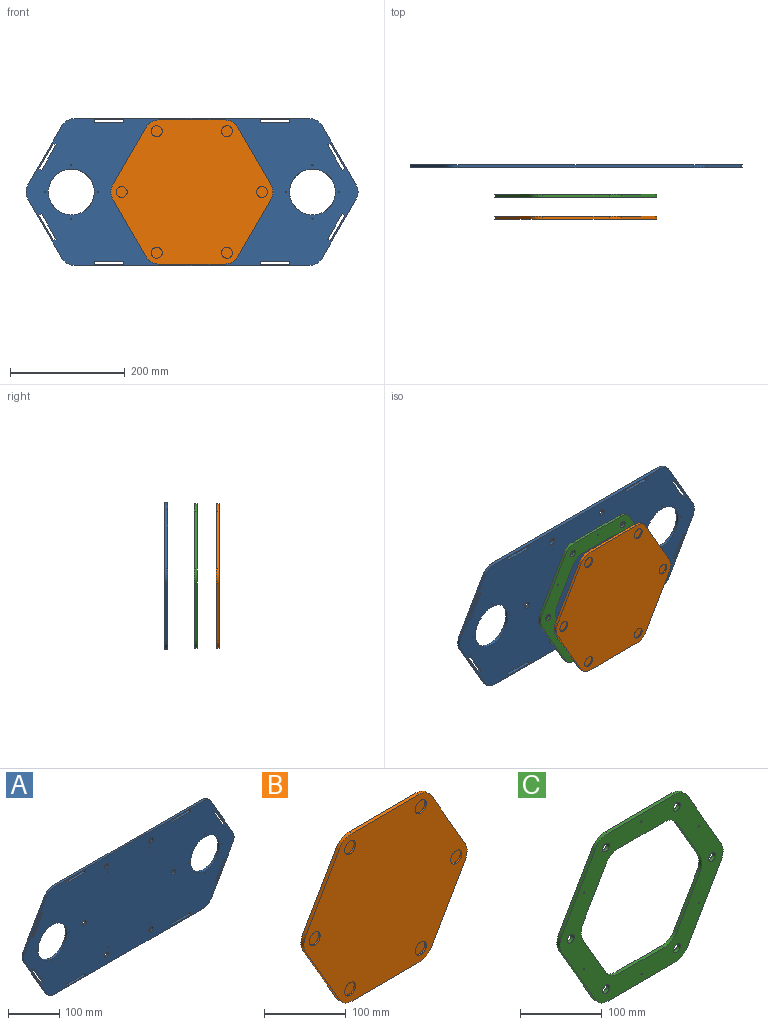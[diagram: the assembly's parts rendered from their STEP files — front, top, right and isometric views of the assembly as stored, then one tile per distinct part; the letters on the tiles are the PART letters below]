
ASSEMBLY  parts=3 mates=3
PART A: 66 faces, bbox 579.1x5.1x256.5 mm
  f0: plane 579.12x256.54mm, normal (0,-1,0), area 118440.4mm2, adj f2,f3,f4,f5,f6,f7,f8,f9
  f1: plane 579.12x256.54mm, normal (0,1,0), area 118440.4mm2, adj f2,f3,f4,f5,f6,f7,f8,f9
  f2: cylinder r=1.02mm len=5.08mm, axis (0,-1,0), area 32.4mm2, adj f0,f1
  f3: cylinder r=1.02mm len=5.08mm, axis (0,-1,0), area 32.4mm2, adj f0,f1
  f4: cylinder r=1.02mm len=5.08mm, axis (0,-1,0), area 32.4mm2, adj f0,f1
  f5: cylinder r=1.02mm len=5.08mm, axis (0,-1,0), area 32.4mm2, adj f0,f1
  f6: cylinder r=5.99mm len=11.99mm, axis (0,-1,0), area 191.3mm2, adj f0,f1
  f7: cylinder r=5.99mm len=11.99mm, axis (0,-1,0), area 191.3mm2, adj f0,f1
  f8: cylinder r=5.99mm len=11.99mm, axis (0,-1,0), area 191.3mm2, adj f0,f1
  f9: cylinder r=5.99mm len=11.99mm, axis (0,-1,0), area 191.3mm2, adj f0,f1
  f10: cylinder r=5.99mm len=11.99mm, axis (0,-1,0), area 191.3mm2, adj f0,f1
  f11: cylinder r=5.99mm len=11.99mm, axis (0,-1,0), area 191.3mm2, adj f0,f1
  f12: cylinder r=40mm len=80mm, axis (0,-1,0), area 1276.7mm2, adj f0,f1
  f13: cylinder r=1.02mm len=5.08mm, axis (0,-1,0), area 32.4mm2, adj f0,f1
  f14: cylinder r=1.02mm len=5.08mm, axis (0,-1,0), area 32.4mm2, adj f0,f1
  f15: cylinder r=1.02mm len=5.08mm, axis (0,-1,0), area 32.4mm2, adj f0,f1
  f16: cylinder r=1.02mm len=5.08mm, axis (0,-1,0), area 32.4mm2, adj f0,f1
  f17: cylinder r=40mm len=80mm, axis (0,-1,0), area 1276.7mm2, adj f0,f1
  f18: cylinder r=1.02mm len=5.08mm, axis (0,-1,0), area 32.4mm2, adj f0,f1
  f19: cylinder r=1.02mm len=5.08mm, axis (0,-1,0), area 32.4mm2, adj f0,f1
  f20: cylinder r=1.02mm len=5.08mm, axis (0,-1,0), area 32.4mm2, adj f0,f1
  f21: cylinder r=1.02mm len=5.08mm, axis (0,-1,0), area 32.4mm2, adj f0,f1
  f22: plane 5.33x5.08mm, normal (-1,0,0), area 27.1mm2, adj f0,f1,f24,f47
  f23: plane 5.33x5.08mm, normal (1,0,0), area 27.1mm2, adj f0,f1,f24,f47
  f24: plane 50.8x5.08mm, normal (0,0,1), area 258.1mm2, adj f0,f1,f22,f23
  f25: plane 5.08x4.62mm, normal (-0.5,0,-0.87), area 27.1mm2, adj f0,f1,f27,f53
  f26: plane 5.08x4.62mm, normal (0.5,0,0.87), area 27.1mm2, adj f0,f1,f27,f53
  f27: plane 43.99x25.4mm, normal (-0.87,0,0.5), area 258.1mm2, adj f0,f1,f25,f26
  f28: plane 5.08x4.62mm, normal (0.5,0,-0.87), area 27.1mm2, adj f0,f1,f30,f52
  f29: plane 5.08x4.62mm, normal (-0.5,0,0.87), area 27.1mm2, adj f0,f1,f30,f52
  f30: plane 43.99x25.4mm, normal (-0.87,0,-0.5), area 258.1mm2, adj f0,f1,f28,f29
  f31: plane 5.33x5.08mm, normal (1,0,0), area 27.1mm2, adj f0,f1,f33,f50
  f32: plane 5.33x5.08mm, normal (-1,0,0), area 27.1mm2, adj f0,f1,f33,f50
  f33: plane 50.8x5.08mm, normal (0,0,-1), area 258.1mm2, adj f0,f1,f31,f32
  f34: plane 5.33x5.08mm, normal (1,0,0), area 27.1mm2, adj f0,f1,f35,f46
  f35: plane 50.8x5.08mm, normal (0,0,1), area 258.1mm2, adj f0,f1,f34,f36
  f36: plane 5.33x5.08mm, normal (-1,0,0), area 27.1mm2, adj f0,f1,f35,f46
  f37: plane 5.08x4.62mm, normal (0.5,0,-0.87), area 27.1mm2, adj f0,f1,f38,f48
  f38: plane 43.99x25.4mm, normal (0.87,0,0.5), area 258.1mm2, adj f0,f1,f37,f39
  f39: plane 5.08x4.62mm, normal (-0.5,0,0.87), area 27.1mm2, adj f0,f1,f38,f48
  f40: plane 5.08x4.62mm, normal (-0.5,0,-0.87), area 27.1mm2, adj f0,f1,f41,f49
  f41: plane 43.99x25.4mm, normal (0.87,0,-0.5), area 258.1mm2, adj f0,f1,f40,f42
  f42: plane 5.08x4.62mm, normal (0.5,0,0.87), area 27.1mm2, adj f0,f1,f41,f49
  f43: plane 5.33x5.08mm, normal (-1,0,0), area 27.1mm2, adj f0,f1,f44,f51
  f44: plane 50.8x5.08mm, normal (0,0,-1), area 258.1mm2, adj f0,f1,f43,f45
  f45: plane 5.33x5.08mm, normal (1,0,0), area 27.1mm2, adj f0,f1,f44,f51
  f46: plane 50.8x5.08mm, normal (0,0,-1), area 258.1mm2, adj f0,f1,f34,f36
  f47: plane 50.8x5.08mm, normal (0,0,-1), area 258.1mm2, adj f0,f1,f22,f23
  f48: plane 43.99x25.4mm, normal (-0.87,0,-0.5), area 258.1mm2, adj f0,f1,f37,f39
  f49: plane 43.99x25.4mm, normal (-0.87,0,0.5), area 258.1mm2, adj f0,f1,f40,f42
  f50: plane 50.8x5.08mm, normal (0,0,1), area 258.1mm2, adj f0,f1,f31,f32
  f51: plane 50.8x5.08mm, normal (0,0,1), area 258.1mm2, adj f0,f1,f43,f45
  f52: plane 43.99x25.4mm, normal (0.87,0,0.5), area 258.1mm2, adj f0,f1,f28,f29
  f53: plane 43.99x25.4mm, normal (0.87,0,-0.5), area 258.1mm2, adj f0,f1,f25,f26
  f54: plane 409.54x5.08mm, normal (0,0,-1), area 2080.5mm2, adj f0,f1,f55,f65
  f55: cylinder r=25.4mm len=22mm, axis (0,-1,0), area 135.1mm2, adj f0,f1,f54,f56
  f56: plane 102.87x59.39mm, normal (0.87,0,-0.5), area 603.4mm2, adj f0,f1,f55,f57
  f57: cylinder r=25.4mm len=25.4mm, axis (0,-1,0), area 135.1mm2, adj f0,f1,f56,f58
  f58: plane 102.87x59.39mm, normal (0.87,0,0.5), area 603.4mm2, adj f0,f1,f57,f59
  f59: cylinder r=25.4mm len=22mm, axis (0,-1,0), area 135.1mm2, adj f0,f1,f58,f60
  f60: plane 409.54x5.08mm, normal (0,0,1), area 2080.5mm2, adj f0,f1,f59,f61
  f61: cylinder r=25.4mm len=22mm, axis (0,-1,0), area 135.1mm2, adj f0,f1,f60,f62
  f62: plane 102.87x59.39mm, normal (-0.87,0,0.5), area 603.4mm2, adj f0,f1,f61,f63
  f63: cylinder r=25.4mm len=25.4mm, axis (0,-1,0), area 135.1mm2, adj f0,f1,f62,f64
  f64: plane 102.87x59.39mm, normal (-0.87,0,-0.5), area 603.4mm2, adj f0,f1,f63,f65
  f65: cylinder r=25.4mm len=22mm, axis (0,-1,0), area 135.1mm2, adj f0,f1,f54,f64
PART B: 26 faces, bbox 282.5x5.1x251.5 mm
  f0: plane 115.85x5.08mm, normal (0,0,-1), area 588.5mm2, adj f1,f11,f12,f13
  f1: cylinder r=25.4mm len=22mm, axis (0,1,0), area 135.1mm2, adj f0,f2,f12,f13
  f2: plane 100.33x57.93mm, normal (0.87,0,-0.5), area 588.5mm2, adj f1,f3,f12,f13
  f3: cylinder r=25.4mm len=25.4mm, axis (0,1,0), area 135.1mm2, adj f2,f4,f12,f13
  f4: plane 100.33x57.93mm, normal (0.87,0,0.5), area 588.5mm2, adj f3,f5,f12,f13
  f5: cylinder r=25.4mm len=22mm, axis (0,1,0), area 135.1mm2, adj f4,f6,f12,f13
  f6: plane 115.85x5.08mm, normal (0,0,1), area 588.5mm2, adj f5,f7,f12,f13
  f7: cylinder r=25.4mm len=22mm, axis (0,1,0), area 135.1mm2, adj f6,f8,f12,f13
  f8: plane 100.33x57.93mm, normal (-0.87,0,0.5), area 588.5mm2, adj f7,f9,f12,f13
  f9: cylinder r=25.4mm len=25.4mm, axis (0,1,0), area 135.1mm2, adj f8,f10,f12,f13
  f10: plane 100.33x57.93mm, normal (-0.87,0,-0.5), area 588.5mm2, adj f9,f11,f12,f13
  f11: cylinder r=25.4mm len=22mm, axis (0,1,0), area 135.1mm2, adj f0,f10,f12,f13
  f12: plane 282.5x251.46mm, normal (0,-1,0), area 52842.4mm2, adj f0,f1,f2,f3,f4,f5,f6,f7
  f13: plane 282.5x251.46mm, normal (0,1,0), area 54552.6mm2, adj f0,f1,f2,f3,f4,f5,f6,f7
  f14: cylinder r=9.53mm len=19.05mm, axis (0,-1,0), area 152mm2, adj f12,f15
  f15: plane 19.05x19.05mm, normal (0,-1,0), area 285mm2, adj f14
  f16: cylinder r=9.53mm len=19.05mm, axis (0,-1,0), area 152mm2, adj f12,f17
  f17: plane 19.05x19.05mm, normal (0,-1,0), area 285mm2, adj f16
  f18: cylinder r=9.53mm len=19.05mm, axis (0,-1,0), area 152mm2, adj f12,f19
  f19: plane 19.05x19.05mm, normal (0,-1,0), area 285mm2, adj f18
  f20: cylinder r=9.53mm len=19.05mm, axis (0,-1,0), area 152mm2, adj f12,f21
  f21: plane 19.05x19.05mm, normal (0,-1,0), area 285mm2, adj f20
  f22: cylinder r=9.53mm len=19.05mm, axis (0,-1,0), area 152mm2, adj f12,f23
  f23: plane 19.05x19.05mm, normal (0,-1,0), area 285mm2, adj f22
  f24: cylinder r=9.53mm len=19.05mm, axis (0,-1,0), area 152mm2, adj f12,f25
  f25: plane 19.05x19.05mm, normal (0,-1,0), area 285mm2, adj f24
PART C: 38 faces, bbox 282.5x5.1x251.5 mm
  f0: cylinder r=25.4mm len=22mm, axis (0,1,0), area 135.1mm2, adj f1,f23,f24,f25
  f1: plane 68.58x39.59mm, normal (0.87,0,0.5), area 402.3mm2, adj f0,f2,f24,f25
  f2: cylinder r=25.4mm len=25.4mm, axis (0,1,0), area 135.1mm2, adj f1,f3,f24,f25
  f3: plane 68.58x39.59mm, normal (0.87,0,-0.5), area 402.3mm2, adj f2,f4,f24,f25
  f4: cylinder r=25.4mm len=22mm, axis (0,1,0), area 135.1mm2, adj f3,f5,f24,f25
  f5: plane 79.19x5.08mm, normal (0,0,-1), area 402.3mm2, adj f4,f6,f24,f25
  f6: cylinder r=25.4mm len=22mm, axis (0,1,0), area 135.1mm2, adj f5,f7,f24,f25
  f7: plane 68.58x39.59mm, normal (-0.87,0,-0.5), area 402.3mm2, adj f6,f8,f24,f25
  f8: cylinder r=25.4mm len=25.4mm, axis (0,1,0), area 135.1mm2, adj f7,f9,f24,f25
  f9: plane 68.58x39.59mm, normal (-0.87,0,0.5), area 402.3mm2, adj f8,f10,f24,f25
  f10: cylinder r=25.4mm len=22mm, axis (0,1,0), area 135.1mm2, adj f9,f23,f24,f25
  f11: plane 115.85x5.08mm, normal (0,0,-1), area 588.5mm2, adj f12,f22,f24,f25
  f12: cylinder r=25.4mm len=22mm, axis (0,1,0), area 135.1mm2, adj f11,f13,f24,f25
  f13: plane 100.33x57.93mm, normal (0.87,0,-0.5), area 588.5mm2, adj f12,f14,f24,f25
  f14: cylinder r=25.4mm len=25.4mm, axis (0,1,0), area 135.1mm2, adj f13,f15,f24,f25
  f15: plane 100.33x57.93mm, normal (0.87,0,0.5), area 588.5mm2, adj f14,f16,f24,f25
  f16: cylinder r=25.4mm len=22mm, axis (0,1,0), area 135.1mm2, adj f15,f17,f24,f25
  f17: plane 115.85x5.08mm, normal (0,0,1), area 588.5mm2, adj f16,f18,f24,f25
  f18: cylinder r=25.4mm len=22mm, axis (0,1,0), area 135.1mm2, adj f17,f19,f24,f25
  f19: plane 100.33x57.93mm, normal (-0.87,0,0.5), area 588.5mm2, adj f18,f20,f24,f25
  f20: cylinder r=25.4mm len=25.4mm, axis (0,1,0), area 135.1mm2, adj f19,f21,f24,f25
  f21: plane 100.33x57.93mm, normal (-0.87,0,-0.5), area 588.5mm2, adj f20,f22,f24,f25
  f22: cylinder r=25.4mm len=22mm, axis (0,1,0), area 135.1mm2, adj f11,f21,f24,f25
  f23: plane 79.19x5.08mm, normal (0,0,1), area 402.3mm2, adj f0,f10,f24,f25
  f24: plane 282.5x251.46mm, normal (0,-1,0), area 23468.1mm2, adj f0,f1,f2,f3,f4,f5,f6,f7
  f25: plane 282.5x251.46mm, normal (0,1,0), area 23468.1mm2, adj f0,f1,f2,f3,f4,f5,f6,f7
  f26: cylinder r=5.99mm len=11.99mm, axis (0,-1,0), area 191.3mm2, adj f24,f25
  f27: cylinder r=5.99mm len=11.99mm, axis (0,-1,0), area 191.3mm2, adj f24,f25
  f28: cylinder r=5.99mm len=11.99mm, axis (0,-1,0), area 191.3mm2, adj f24,f25
  f29: cylinder r=5.99mm len=11.99mm, axis (0,-1,0), area 191.3mm2, adj f24,f25
  f30: cylinder r=5.99mm len=11.99mm, axis (0,-1,0), area 191.3mm2, adj f24,f25
  f31: cylinder r=5.99mm len=11.99mm, axis (0,-1,0), area 191.3mm2, adj f24,f25
  f32: cylinder r=1.02mm len=5.08mm, axis (0,-1,0), area 32.4mm2, adj f24,f25
  f33: cylinder r=1.02mm len=5.08mm, axis (0,-1,0), area 32.4mm2, adj f24,f25
  f34: cylinder r=1.02mm len=5.08mm, axis (0,-1,0), area 32.4mm2, adj f24,f25
  f35: cylinder r=1.02mm len=5.08mm, axis (0,-1,0), area 32.4mm2, adj f24,f25
  f36: cylinder r=1.02mm len=5.08mm, axis (0,-1,0), area 32.4mm2, adj f24,f25
  f37: cylinder r=1.02mm len=5.08mm, axis (0,-1,0), area 32.4mm2, adj f24,f25
PLACE A t=(-468.79,71.47,-204.75)mm
PLACE B t=(-323.61,-18.6,-204.75)mm
PLACE C t=(-323.61,19.92,-204.75)mm
MATE cylindrical C.f26 <-> A.f6  axis (0,-1,0) through (-384.85,14.84,-98.67)mm
MATE planar B.f4 <-> C.f15  axis (0.87,0,0.5) through (-214.72,-21.14,-141.89)mm
MATE planar B.f6 <-> C.f17  axis (0,0,1) through (-323.61,-21.14,-79.02)mm
